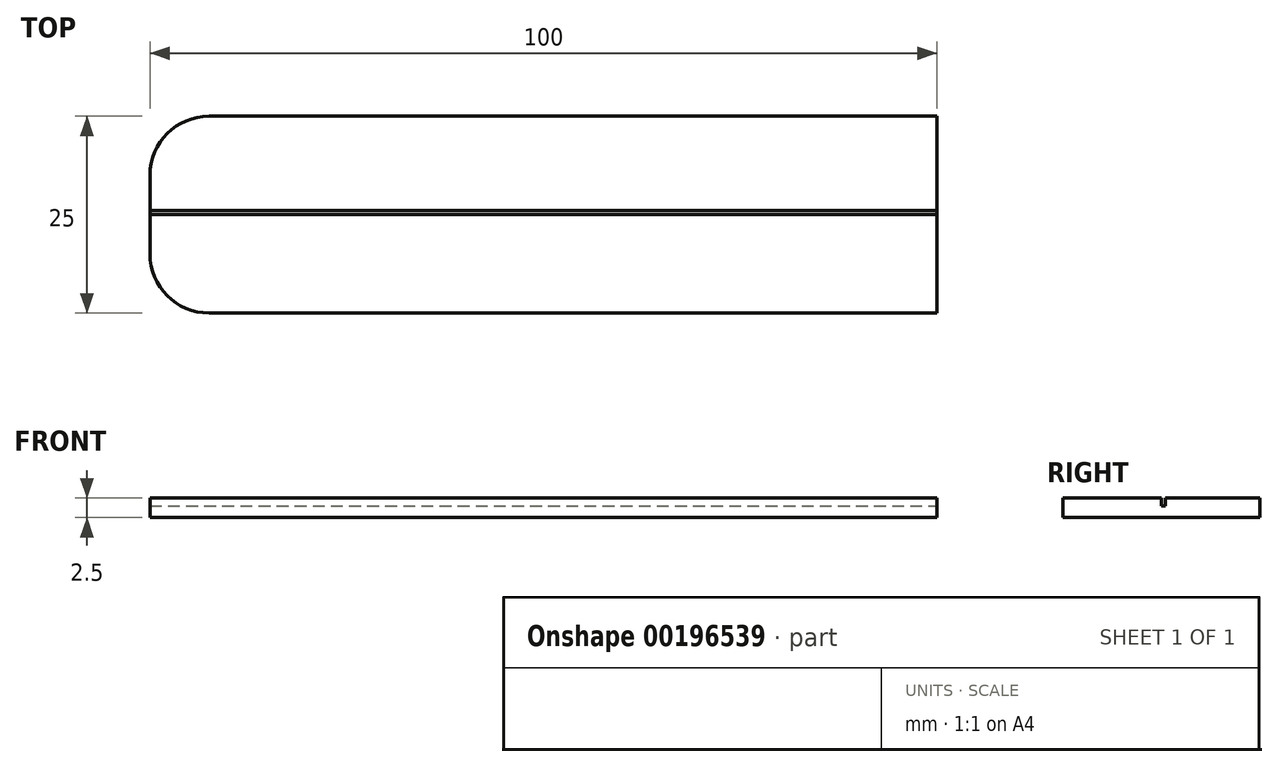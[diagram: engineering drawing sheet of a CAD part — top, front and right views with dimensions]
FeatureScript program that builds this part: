
annotation { "Feature Type Name" : "Feature", "Feature Type Description" : "" }
export const myFeature = defineFeature(function(context is Context, id is Id, definition is map)
    precondition{}
    {
        {
            var Q0;
            Q0=qCreatedBy(makeId("Top.planeOp"),FACE);
            var sketch = newSketch(context, id + "F0", { "sketchPlane" : qUnion([Q0])});
            skLineSegment(sketch, "E0.bottom", {"start": v(-46.25, 0) * mm, "end": v(46.25, 0) * mm});
            skLineSegment(sketch, "E0.top", {"start": v(-46.25, 25) * mm, "end": v(46.25, 25) * mm});
            skLineSegment(sketch, "E0.left", {"start": v(-53.75, 7.5) * mm, "end": v(-53.75, 17.5) * mm});
            skLineSegment(sketch, "E0.right", {"start": v(46.25, 0) * mm, "end": v(46.25, 25) * mm});
            skPoint(sketch, "E1.visualSharp", {"position": v(-53.75, 25) * mm});
            skArc(sketch, "E1.filletArc", {"start": v(-46.25, 25) * mm, "mid": v(-51.55, 22.8) * mm, "end": v(-53.75, 17.5) * mm});
            skPoint(sketch, "E2.visualSharp", {"position": v(-53.75, 0) * mm});
            skArc(sketch, "E2.filletArc", {"start": v(-53.75, 7.5) * mm, "mid": v(-51.55, 2.2) * mm, "end": v(-46.25, 0) * mm});
            skSolve(sketch);
        }
        {
            var Q0;
            Q0 = qSketchRegion(id + "F0", true);
            extrude(context, id + "F1", {"entities" : qUnion([Q0]), "depth" : 2.5 * mm});
        }
        {
            var Q0;
            Q0=makeQuery(id+"F1.opExtrude","CAP_FACE",FACE,{"disambiguationData":[OSD([sQuery(id+"F0.wireOp",EDGE,"E0.bottom"),sQuery(id+"F0.wireOp",EDGE,"E0.top"),sQuery(id+"F0.wireOp",EDGE,"E0.left"),sQuery(id+"F0.wireOp",EDGE,"E0.right"),sQuery(id+"F0.wireOp",EDGE,"E1.filletArc"),sQuery(id+"F0.wireOp",EDGE,"E2.filletArc")])],"isStart":false});
            var sketch = newSketch(context, id + "F2", { "sketchPlane" : qUnion([Q0])});
            skLineSegment(sketch, "E3.bottom", {"start": v(-53.75, 12.5) * mm, "end": v(46.25, 12.5) * mm});
            skLineSegment(sketch, "E3.top", {"start": v(-53.75, 13) * mm, "end": v(46.25, 13) * mm});
            skLineSegment(sketch, "E3.left", {"start": v(-53.75, 12.5) * mm, "end": v(-53.75, 13) * mm});
            skLineSegment(sketch, "E3.right", {"start": v(46.25, 12.5) * mm, "end": v(46.25, 13) * mm});
            skSolve(sketch);
        }
        {
            var Q0;
            Q0 = qSketchRegion(id + "F2", true);
            extrude(context, id + "F3", {"entities" : qUnion([Q0]), "operationType" : NewBodyOperationType.REMOVE, "oppositeDirection" : true, "depth" : 1 * mm});
        }
    });
